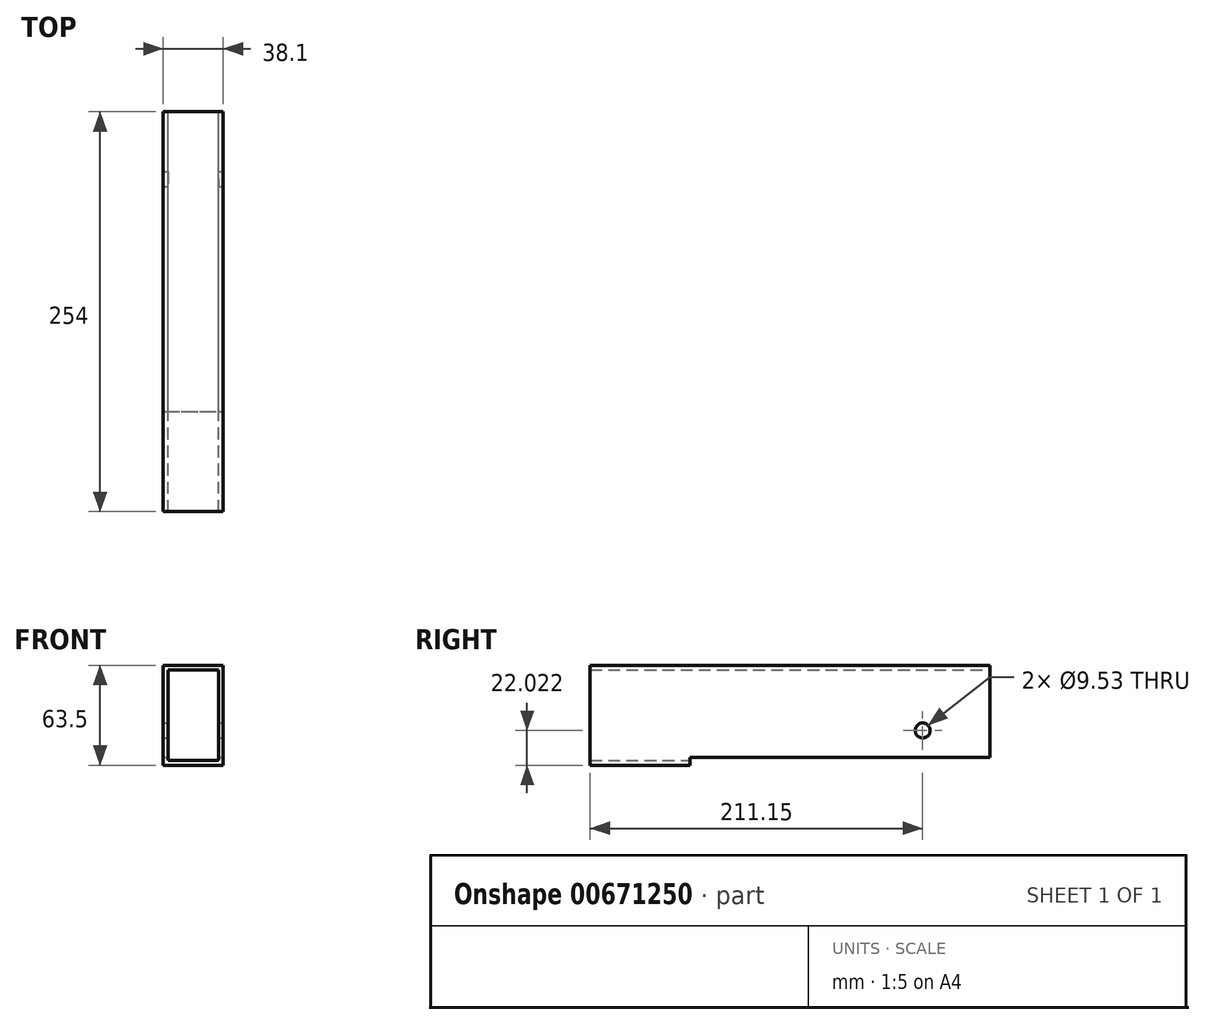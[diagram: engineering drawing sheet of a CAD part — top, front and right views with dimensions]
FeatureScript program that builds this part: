
annotation { "Feature Type Name" : "Feature", "Feature Type Description" : "" }
export const myFeature = defineFeature(function(context is Context, id is Id, definition is map)
    precondition{}
    {
        {
            var Q0;
            Q0=qCreatedBy(makeId("Front.planeOp"),FACE);
            var sketch = newSketch(context, id + "F0", { "sketchPlane" : qUnion([Q0])});
            skLineSegment(sketch, "E0.bottom", {"start": v(19.05, -31.75) * mm, "end": v(-19.05, -31.75) * mm});
            skLineSegment(sketch, "E0.top", {"start": v(19.05, 31.75) * mm, "end": v(-19.05, 31.75) * mm});
            skLineSegment(sketch, "E0.left", {"start": v(19.05, -31.75) * mm, "end": v(19.05, 31.75) * mm});
            skLineSegment(sketch, "E0.right", {"start": v(-19.05, -31.75) * mm, "end": v(-19.05, 31.75) * mm});
            skPoint(sketch, "E0.middle", {"position": v(0, 0) * mm});
            skLineSegment(sketch, "E1.0", {"start": v(-16, -28.7) * mm, "end": v(-16, 28.7) * mm});
            skLineSegment(sketch, "E1.1", {"start": v(16, -28.7) * mm, "end": v(-16, -28.7) * mm});
            skLineSegment(sketch, "E1.2", {"start": v(16, -28.7) * mm, "end": v(16, 28.7) * mm});
            skLineSegment(sketch, "E1.3", {"start": v(16, 28.7) * mm, "end": v(-16, 28.7) * mm});
            skSolve(sketch);
        }
        {
            var Q0;
            Q0=makeQuery(id+"F0.imprint","IMPRINT",FACE,{"disambiguationData":[TD([[makeQuery(id+"F0.imprint","IMPRINT",EDGE,{"derivedFrom":sQuery(id+"F0.wireOp",EDGE,"E0.bottom")}),-1.0]])]});
            extrude(context, id + "F1", {"entities" : qUnion([Q0]), "depth" : 254 * mm, "offsetDistance" : 25.4 * mm});
        }
        {
            var Q0;
            Q0=makeQuery(id+"F1.opExtrude","SWEPT_FACE",FACE,{"disambiguationData":[OSD([sQuery(id+"F0.wireOp",EDGE,"E0.left")])]});
            var sketch = newSketch(context, id + "F2", { "sketchPlane" : qUnion([Q0])});
            skLineSegment(sketch, "E2.bottom", {"start": v(0, -31.75) * mm, "end": v(-190.5, -31.75) * mm});
            skLineSegment(sketch, "E2.top", {"start": v(0, -26.67) * mm, "end": v(-190.5, -26.67) * mm});
            skLineSegment(sketch, "E2.left", {"start": v(0, -31.75) * mm, "end": v(0, -26.67) * mm});
            skLineSegment(sketch, "E2.right", {"start": v(-190.5, -31.75) * mm, "end": v(-190.5, -26.67) * mm});
            skCircle(sketch, "E3", {"center": v(-42.85, -9.73) * mm, "radius": 4.76 * mm});
            skSolve(sketch);
        }
        {
            var Q0;
            Q0=makeQuery(id+"F2.imprint","IMPRINT",FACE,{"disambiguationData":[TD([[makeQuery(id+"F2.imprint","IMPRINT",EDGE,{"derivedFrom":sQuery(id+"F2.wireOp",EDGE,"E2.bottom")}),1.0]])]});
            var Q1;
            Q1=makeQuery(id+"F2.imprint","IMPRINT",FACE,{"disambiguationData":[TD([[makeQuery(id+"F2.imprint","IMPRINT",EDGE,{"derivedFrom":sQuery(id+"F2.wireOp",EDGE,"E3")}),1.0]])]});
            extrude(context, id + "F3", {"entities" : qUnion([Q0, Q1]), "operationType" : NewBodyOperationType.REMOVE, "oppositeDirection" : true, "depth" : 50.8 * mm, "offsetDistance" : 25.4 * mm});
        }
    });
